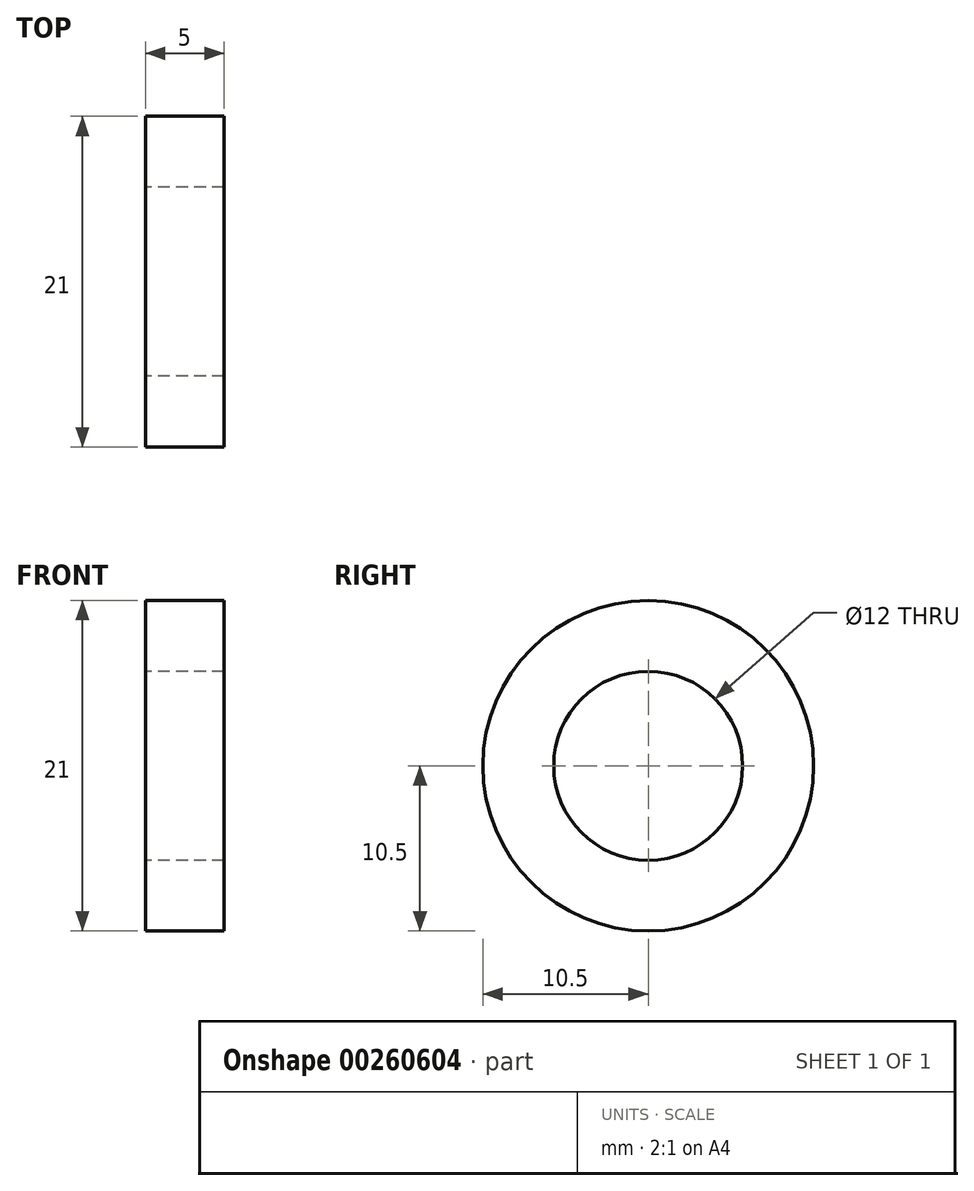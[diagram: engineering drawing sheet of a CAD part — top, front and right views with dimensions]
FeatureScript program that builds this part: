
annotation { "Feature Type Name" : "Feature", "Feature Type Description" : "" }
export const myFeature = defineFeature(function(context is Context, id is Id, definition is map)
    precondition{}
    {
        {
            var Q0;
            Q0=qCreatedBy(makeId("Right.planeOp"),FACE);
            var sketch = newSketch(context, id + "F0", { "sketchPlane" : qUnion([Q0])});
            skCircle(sketch, "E0", {"center": v(0, 0) * mm, "radius": 10.5 * mm});
            skCircle(sketch, "E1", {"center": v(0, 0) * mm, "radius": 6 * mm});
            skSolve(sketch);
        }
        {
            var Q0;
            Q0=makeQuery(id+"F0.imprint","IMPRINT",FACE,{"disambiguationData":[TD([[makeQuery(id+"F0.imprint","IMPRINT",EDGE,{"derivedFrom":sQuery(id+"F0.wireOp",EDGE,"E0")}),1.0]])]});
            extrude(context, id + "F1", {"entities" : qUnion([Q0]), "depth" : 5 * mm});
        }
    });
